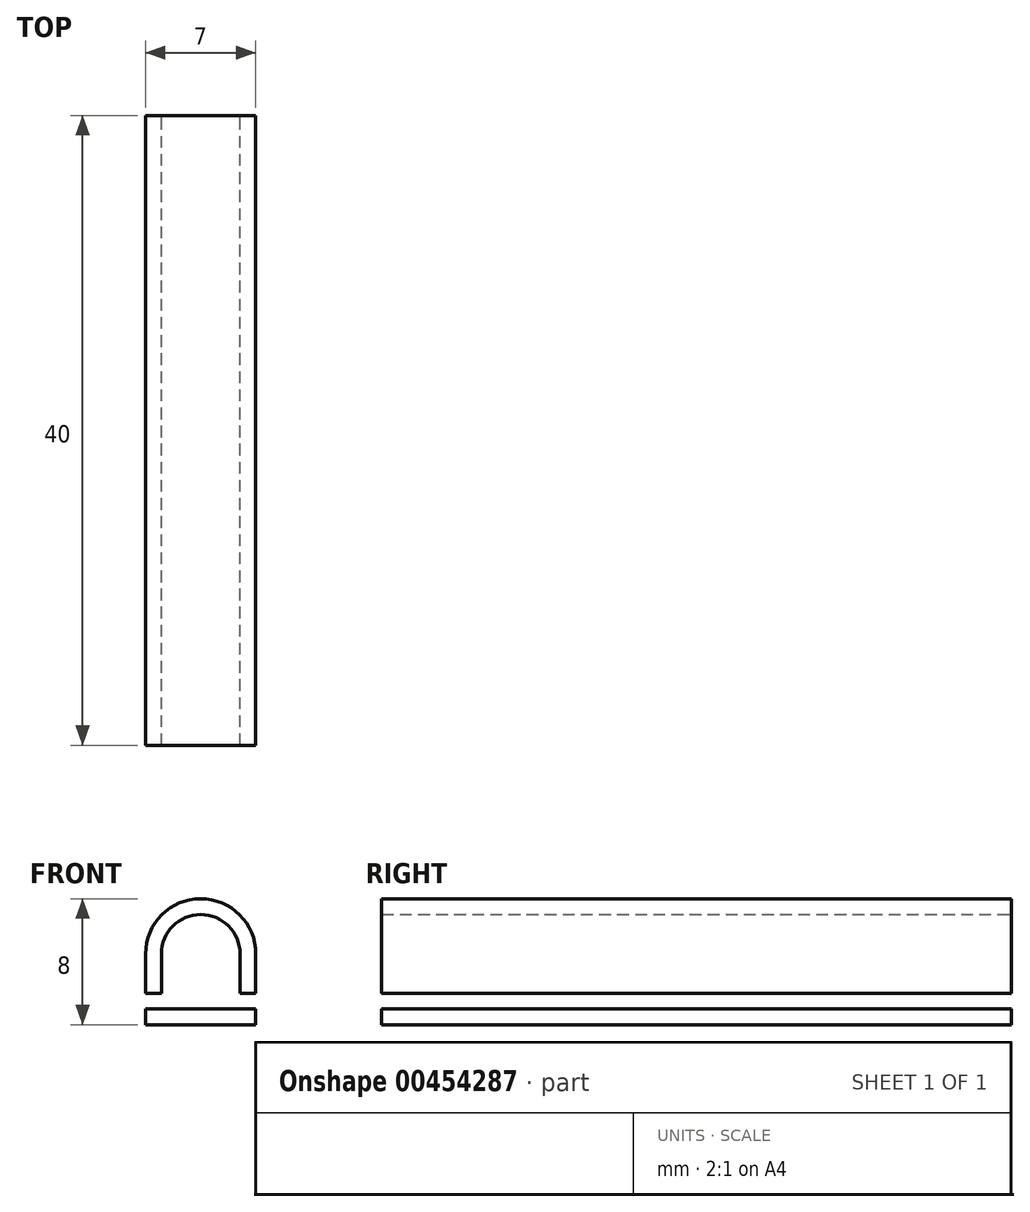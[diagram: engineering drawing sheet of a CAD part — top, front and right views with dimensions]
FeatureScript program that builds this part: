
annotation { "Feature Type Name" : "Feature", "Feature Type Description" : "" }
export const myFeature = defineFeature(function(context is Context, id is Id, definition is map)
    precondition{}
    {
        {
            var Q0;
            Q0=qCreatedBy(makeId("Front.planeOp"),FACE);
            var sketch = newSketch(context, id + "F0", { "sketchPlane" : qUnion([Q0])});
            skLineSegment(sketch, "E0", {"start": v(0, 0) * mm, "end": v(0, 32.3) * mm});
            skSolve(sketch);
        }
        {
            var Q0;
            Q0=qCreatedBy(makeId("Front.planeOp"),FACE);
            var Q1;
            Q1 = qBodyType(qCreatedBy(id + "F0" ,EDGE), BodyType.WIRE);
            cPlane(context, id + "F1", {"entities" : qUnion([Q0, Q1]), "cplaneType" : CPlaneType.LINE_ANGLE, "offset" : 25 * mm, "angle" : 45 * degree, "width" : 150 * mm, "height" : 150 * mm});
        }
        {
            var Q0;
            Q0=qCreatedBy(makeId("Front.planeOp"),FACE);
            var Q1;
            Q1 = qBodyType(qCreatedBy(id + "F0" ,EDGE), BodyType.WIRE);
            cPlane(context, id + "F2", {"entities" : qUnion([Q0, Q1]), "cplaneType" : CPlaneType.LINE_ANGLE, "offset" : 25 * mm, "angle" : 135 * degree, "width" : 150 * mm, "height" : 150 * mm});
        }
        {
            var Q0;
            Q0=qCreatedBy(makeId("Front.planeOp"),FACE);
            var sketch = newSketch(context, id + "F3", { "sketchPlane" : qUnion([Q0])});
            skLineSegment(sketch, "E1", {"start": v(2.5, 0) * mm, "end": v(3.5, 0) * mm});
            skLineSegment(sketch, "E2", {"start": v(2.5, 0) * mm, "end": v(2.5, 2.5) * mm});
            skArc(sketch, "E3", {"start": v(2.5, 2.5) * mm, "mid": v(0, 5) * mm, "end": v(-2.5, 2.5) * mm});
            skLineSegment(sketch, "E4", {"start": v(-2.5, 2.5) * mm, "end": v(-2.5, 0) * mm});
            skLineSegment(sketch, "E5", {"start": v(3.5, 0) * mm, "end": v(3.5, 2.5) * mm});
            skArc(sketch, "E6", {"start": v(3.5, 2.5) * mm, "mid": v(0, 6) * mm, "end": v(-3.5, 2.5) * mm});
            skLineSegment(sketch, "E7", {"start": v(-3.5, 2.5) * mm, "end": v(-3.5, 0) * mm});
            skLineSegment(sketch, "E8", {"start": v(-3.5, 0) * mm, "end": v(-2.5, 0) * mm});
            skLineSegment(sketch, "E9", {"start": v(0, -1) * mm, "end": v(-3.5, -1) * mm});
            skLineSegment(sketch, "E10", {"start": v(-3.5, -1) * mm, "end": v(-3.5, -2) * mm});
            skLineSegment(sketch, "E11", {"start": v(-3.5, -2) * mm, "end": v(3.5, -2) * mm});
            skLineSegment(sketch, "E12", {"start": v(3.5, -2) * mm, "end": v(3.5, -1) * mm});
            skLineSegment(sketch, "E13", {"start": v(3.5, -1) * mm, "end": v(0, -1) * mm});
            skSolve(sketch);
        }
        {
            var Q0;
            Q0 = qSketchRegion(id + "F3", true);
            extrude(context, id + "F4", {"entities" : qUnion([Q0]), "depth" : 40 * mm});
        }
    });
